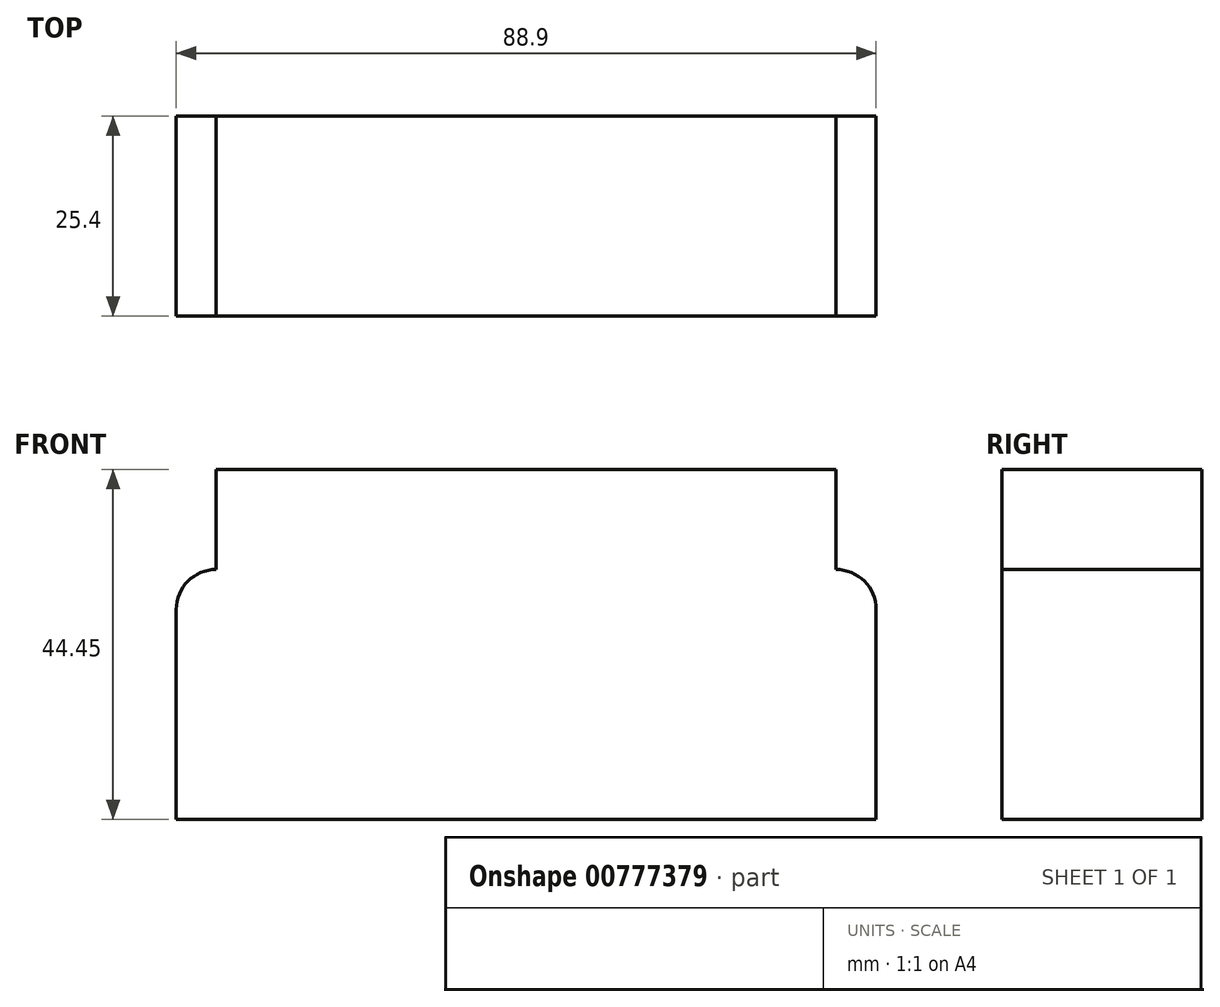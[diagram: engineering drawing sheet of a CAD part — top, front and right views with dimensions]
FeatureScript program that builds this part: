
annotation { "Feature Type Name" : "Feature", "Feature Type Description" : "" }
export const myFeature = defineFeature(function(context is Context, id is Id, definition is map)
    precondition{}
    {
        {
            var Q0;
            Q0=qCreatedBy(makeId("Front.planeOp"),FACE);
            var sketch = newSketch(context, id + "F0", { "sketchPlane" : qUnion([Q0])});
            skLineSegment(sketch, "E0.bottom", {"start": v(-88.9, 10.51) * mm, "end": v(0, 10.51) * mm});
            skLineSegment(sketch, "E0.top", {"start": v(-88.9, -21.24) * mm, "end": v(0, -21.24) * mm});
            skLineSegment(sketch, "E0.left", {"start": v(-88.9, 10.51) * mm, "end": v(-88.9, -21.24) * mm});
            skLineSegment(sketch, "E0.right", {"start": v(0, 10.51) * mm, "end": v(0, -21.24) * mm});
            skSolve(sketch);
        }
        {
            var Q0;
            Q0=makeQuery(id+"F0.imprint","IMPRINT",FACE,{"disambiguationData":[TD([[makeQuery(id+"F0.imprint","IMPRINT",EDGE,{"derivedFrom":sQuery(id+"F0.wireOp",EDGE,"E0.bottom")}),-1.0]])]});
            extrude(context, id + "F1", {"entities" : qUnion([Q0]), "depth" : 25.4 * mm, "offsetDistance" : 25.4 * mm});
        }
        {
            var Q0;
            Q0=makeQuery(id+"F1.opExtrude","SWEPT_EDGE",EDGE,{"disambiguationData":[OSD([sQuery(id+"F0.wireOp",EDGE,"E0.bottom"),sQuery(id+"F0.wireOp",EDGE,"E0.left")])]});
            var Q1;
            Q1=makeQuery(id+"F1.opExtrude","SWEPT_EDGE",EDGE,{"disambiguationData":[OSD([sQuery(id+"F0.wireOp",EDGE,"E0.bottom"),sQuery(id+"F0.wireOp",EDGE,"E0.right")])]});
            fillet(context, id + "F2", {"entities" : qUnion([Q0, Q1]), "radius" : 5.08 * mm, "tangentPropagation" : true, "allowEdgeOverflow" : false});
        }
        {
            var Q0;
            Q0=makeQuery(id+"F1.opExtrude","SWEPT_FACE",FACE,{"disambiguationData":[OSD([sQuery(id+"F0.wireOp",EDGE,"E0.bottom")])]});
            extrude(context, id + "F3", {"entities" : qUnion([Q0]), "operationType" : NewBodyOperationType.ADD, "depth" : 12.7 * mm, "offsetDistance" : 25.4 * mm});
        }
    });
